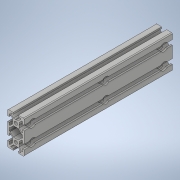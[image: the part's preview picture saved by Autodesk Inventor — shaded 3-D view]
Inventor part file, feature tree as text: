
AUTODESK INVENTOR PART (.ipt)
format: ipt  version: 2022 (Build 260153000, 153)  size: 409,088 bytes
history: native  units: mm
features: other x10, revolve x6, sketch x5, extrude x1, hole x1, pattern_linear x1
ambient origin geometry x8: Origin, YZ Plane, XZ Plane, XY Plane, X Axis, Y Axis, Z Axis, Center Point
bodies: Solid1 (feature_tree)
feature tree (24):
  extrude  "Extrusion1"  Depth=10.0mm TaperAngle=0.0deg
  hole  "Hole1"  [1 undecoded]
  pattern_linear  "Rectangular Pattern1"  Spacing1=360.0deg  [1 undecoded]
  revolve  "Revolution1"  Angle=360.0deg
  revolve  "Revolution2"  [1 undecoded]
  revolve  "Revolution3"  [1 undecoded]
  revolve  "Revolution4"  [1 undecoded]
  revolve  "Revolution5"  [1 undecoded]
  revolve  "Revolution6"  [1 undecoded]
  other  "C1_XY"
  other  "C1_YZ"
  other  "C1_ZX"
  other  "C1_X"
  other  "C1_Y"
  other  "C1_Z"
  other  "C1_Center"
  sketch  "Sketch_1"  dims[d0=180.0mm d1=0.0mm]
  sketch  "Sketch2"  dims[d2=4.2mm d3=6.0mm d4=4.0mm d5=2.0mm d6=90.0deg d7=180.0mm d8=0.0mm d9=20.0mm d11=20.0mm d12=10.0mm d14=0.0mm]
  sketch  "Sketch_50"  dims[d15=360.0deg d16=360.0deg]
  other  "_p_______27_Sketch_50_0"
  sketch  "Sketch_51"  dims[d17=360.0deg]
  other  "_p_______28_Sketch_51_0"
  sketch  "Sketch_52"  dims[d18=360.0deg d19=360.0deg d20=360.0deg d21=0.0mm]
  other  "_p_______29_Sketch_52_0"
note: 7 required parameter values undecoded (feature->parameter linkage not recoverable at this tier; creation-order binding heuristic only, values carry confidence <= 0.55)